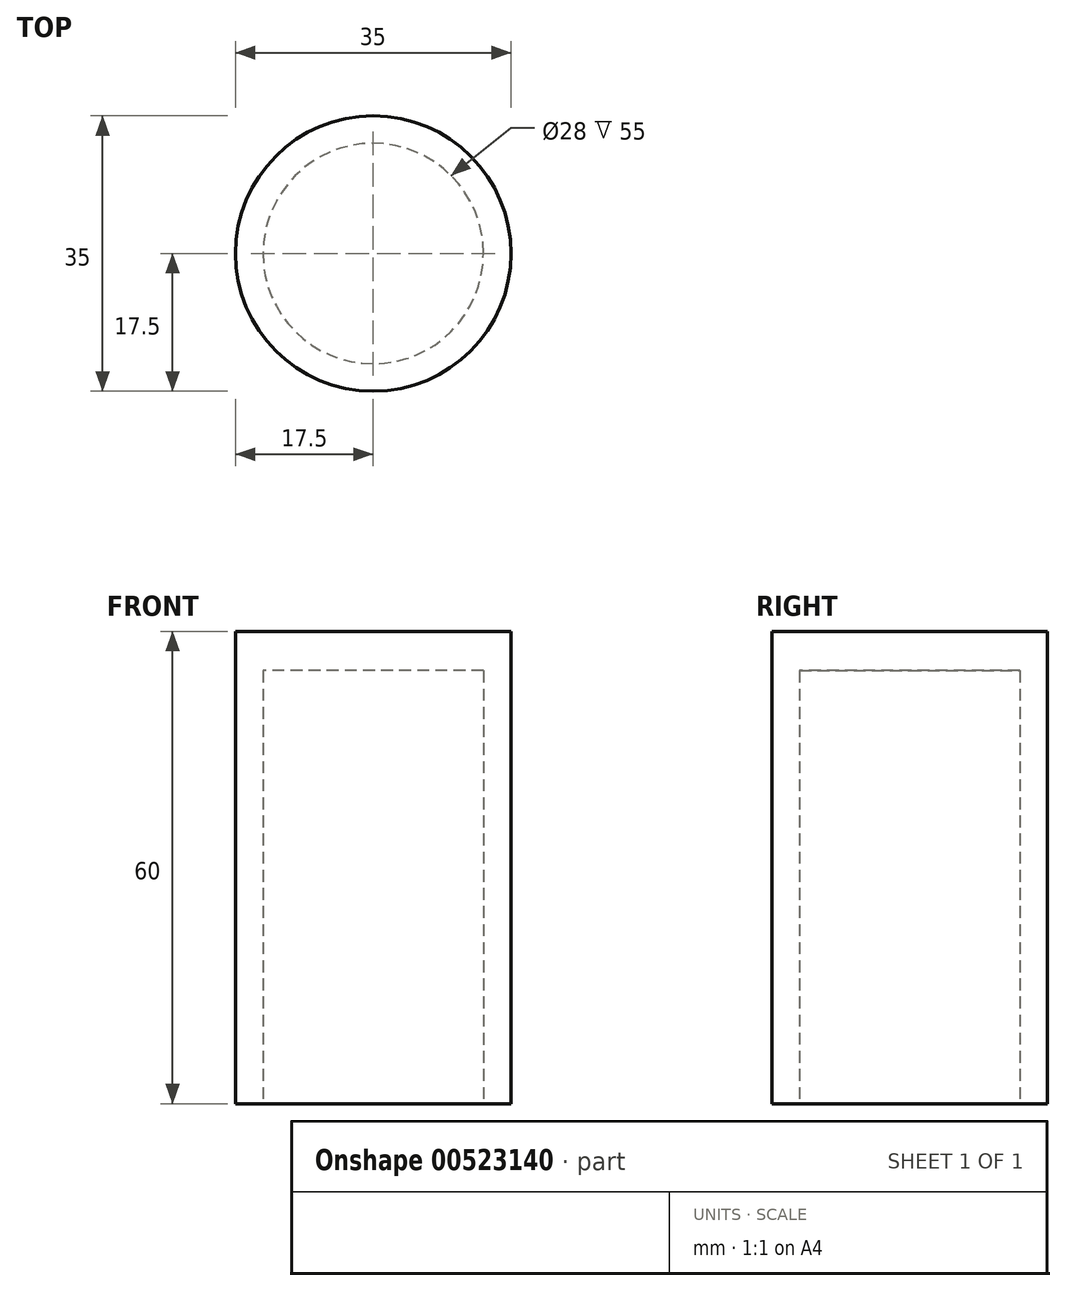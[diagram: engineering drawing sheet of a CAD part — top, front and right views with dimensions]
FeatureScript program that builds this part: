
annotation { "Feature Type Name" : "Feature", "Feature Type Description" : "" }
export const myFeature = defineFeature(function(context is Context, id is Id, definition is map)
    precondition{}
    {
        {
            var Q0;
            Q0=qCreatedBy(makeId("Top.planeOp"),FACE);
            var sketch = newSketch(context, id + "F0", { "sketchPlane" : qUnion([Q0])});
            skCircle(sketch, "E0", {"center": v(0, 0) * mm, "radius": 14 * mm});
            skSolve(sketch);
        }
        {
            var Q0;
            Q0=qCreatedBy(makeId("Top.planeOp"),FACE);
            var sketch = newSketch(context, id + "F1", { "sketchPlane" : qUnion([Q0])});
            skCircle(sketch, "E1", {"center": v(0, 0) * mm, "radius": 17.5 * mm});
            skSolve(sketch);
        }
        {
            var Q0;
            Q0=qSketchRegion(id+"F1",true);
            extrude(context, id + "F2", {"entities" : qUnion([Q0]), "depth" : 60 * mm, "offsetDistance" : 25 * mm});
        }
        {
            var Q0;
            Q0=qSketchRegion(id+"F0",true);
            extrude(context, id + "F3", {"entities" : qUnion([Q0]), "operationType" : NewBodyOperationType.REMOVE, "depth" : 55 * mm, "offsetDistance" : 25 * mm});
        }
    });
